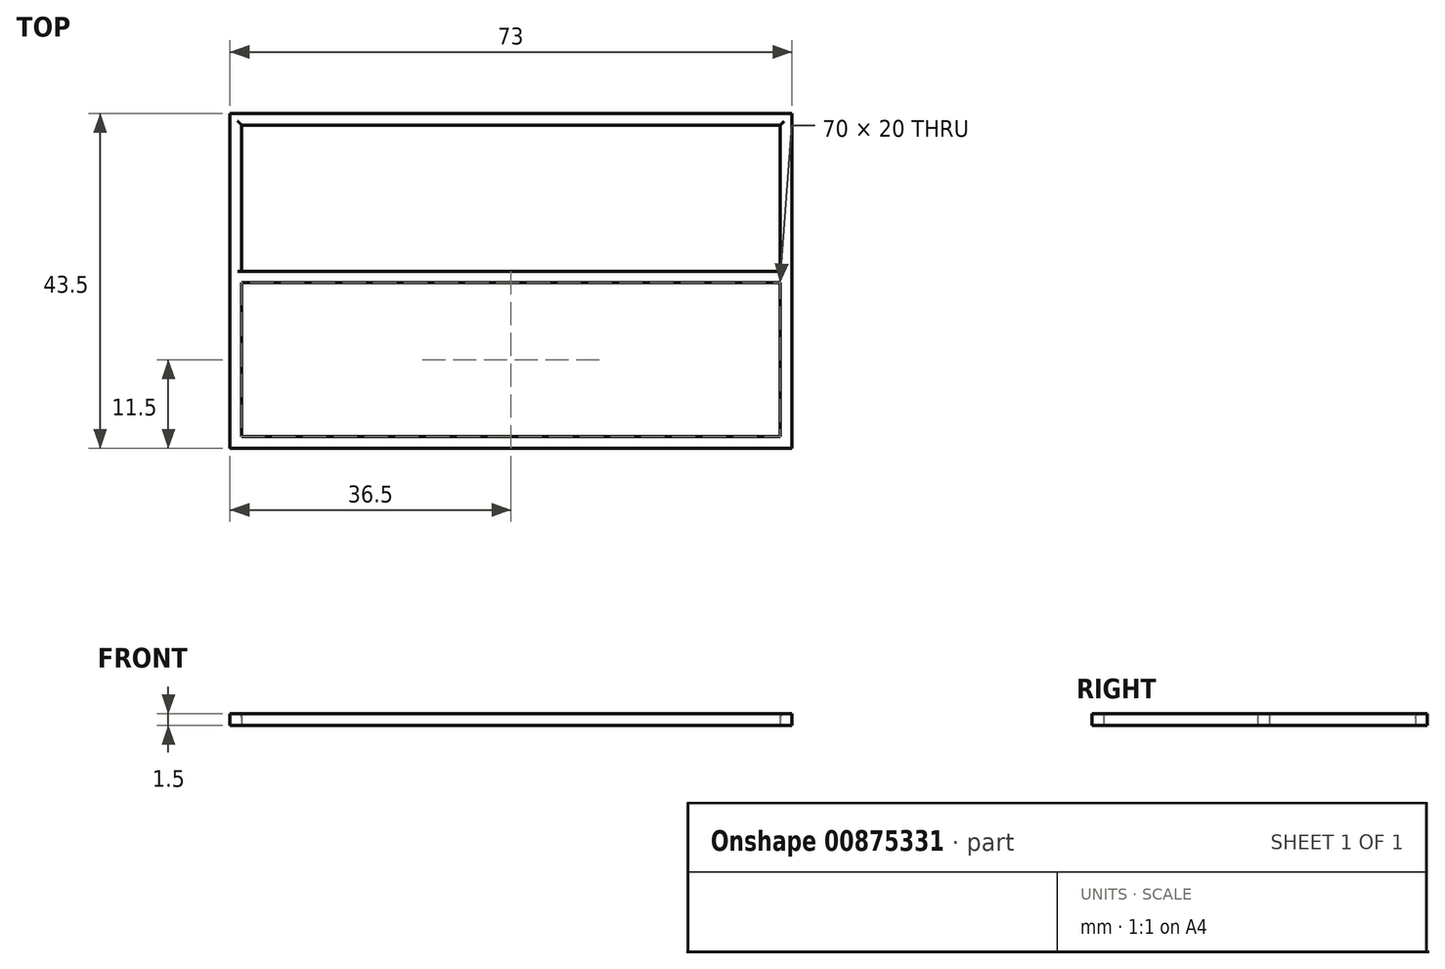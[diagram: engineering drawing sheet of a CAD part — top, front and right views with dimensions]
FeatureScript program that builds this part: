
annotation { "Feature Type Name" : "Feature", "Feature Type Description" : "" }
export const myFeature = defineFeature(function(context is Context, id is Id, definition is map)
    precondition{}
    {
        {
            var Q0;
            Q0=qCreatedBy(makeId("Top.planeOp"),FACE);
            var sketch = newSketch(context, id + "F0", { "sketchPlane" : qUnion([Q0])});
            skLineSegment(sketch, "E0.bottom", {"start": v(0, 0) * mm, "end": v(73, 0) * mm});
            skLineSegment(sketch, "E0.top", {"start": v(0, 43.5) * mm, "end": v(73, 43.5) * mm});
            skLineSegment(sketch, "E0.left", {"start": v(0, 0) * mm, "end": v(0, 43.5) * mm});
            skLineSegment(sketch, "E0.right", {"start": v(73, 0) * mm, "end": v(73, 43.5) * mm});
            skLineSegment(sketch, "E1.bottom", {"start": v(1.5, 42) * mm, "end": v(71.5, 42) * mm});
            skLineSegment(sketch, "E1.top", {"start": v(1.5, 1.5) * mm, "end": v(71.5, 1.5) * mm});
            skLineSegment(sketch, "E1.left", {"start": v(1.5, 42) * mm, "end": v(1.5, 1.5) * mm});
            skLineSegment(sketch, "E1.right", {"start": v(71.5, 42) * mm, "end": v(71.5, 1.5) * mm});
            skLineSegment(sketch, "E2.bottom", {"start": v(1.5, 23) * mm, "end": v(71.5, 23) * mm});
            skLineSegment(sketch, "E2.top", {"start": v(1.5, 21.5) * mm, "end": v(71.5, 21.5) * mm});
            skLineSegment(sketch, "E2.left", {"start": v(1.5, 23) * mm, "end": v(1.5, 21.5) * mm});
            skLineSegment(sketch, "E2.right", {"start": v(71.5, 23) * mm, "end": v(71.5, 21.5) * mm});
            skSolve(sketch);
        }
        {
            var Q0;
            Q0=makeQuery(id+"F0.imprint","IMPRINT",FACE,{"disambiguationData":[TD([[makeQuery(id+"F0.imprint","IMPRINT",EDGE,{"derivedFrom":sQuery(id+"F0.wireOp",EDGE,"E0.bottom")}),1.0]])]});
            var Q1;
            Q1=makeQuery(id+"F0.imprint","IMPRINT",FACE,{"disambiguationData":[TD([[makeQuery(id+"F0.imprint","IMPRINT",EDGE,{"derivedFrom":sQuery(id+"F0.wireOp",EDGE,"E2.bottom")}),-1.0]])]});
            extrude(context, id + "F1", {"entities" : qUnion([Q0, Q1]), "depth" : 1.5 * mm, "offsetDistance" : 25 * mm});
        }
        {
            var Q0;
            {var subQ0=sQuery(id+"F0.wireOp",EDGE,"E1.right");Q0=makeQuery(id+"F1.opExtrude","CAP_EDGE",EDGE,{"disambiguationData":[OSD([subQ0]),TDD([makeQuery(id+"F0.imprint","IMPRINT",EDGE,{"disambiguationData":[TD([[makeQuery(id+"F0.imprint","INTERSECT",VERTEX,{"derivedFrom":[sQuery(id+"F0.wireOp",EDGE,"E1.bottom"),subQ0]}),-1.0]])],"derivedFrom":subQ0})])],"isStart":false});}
            var Q1;
            Q1=makeQuery(id+"F1.opExtrude","CAP_EDGE",EDGE,{"disambiguationData":[OSD([sQuery(id+"F0.wireOp",EDGE,"E1.bottom")])],"isStart":false});
            var Q2;
            {var subQ0=sQuery(id+"F0.wireOp",EDGE,"E1.left");Q2=makeQuery(id+"F1.opExtrude","CAP_EDGE",EDGE,{"disambiguationData":[OSD([subQ0]),TDD([makeQuery(id+"F0.imprint","IMPRINT",EDGE,{"disambiguationData":[TD([[makeQuery(id+"F0.imprint","INTERSECT",VERTEX,{"derivedFrom":[sQuery(id+"F0.wireOp",EDGE,"E1.bottom"),subQ0]}),-1.0]])],"derivedFrom":subQ0})])],"isStart":false});}
            fillet(context, id + "F2", {"entities" : qUnion([Q0, Q1, Q2]), "radius" : 0.5 * mm, "tangentPropagation" : true, "allowEdgeOverflow" : false});
        }
    });
